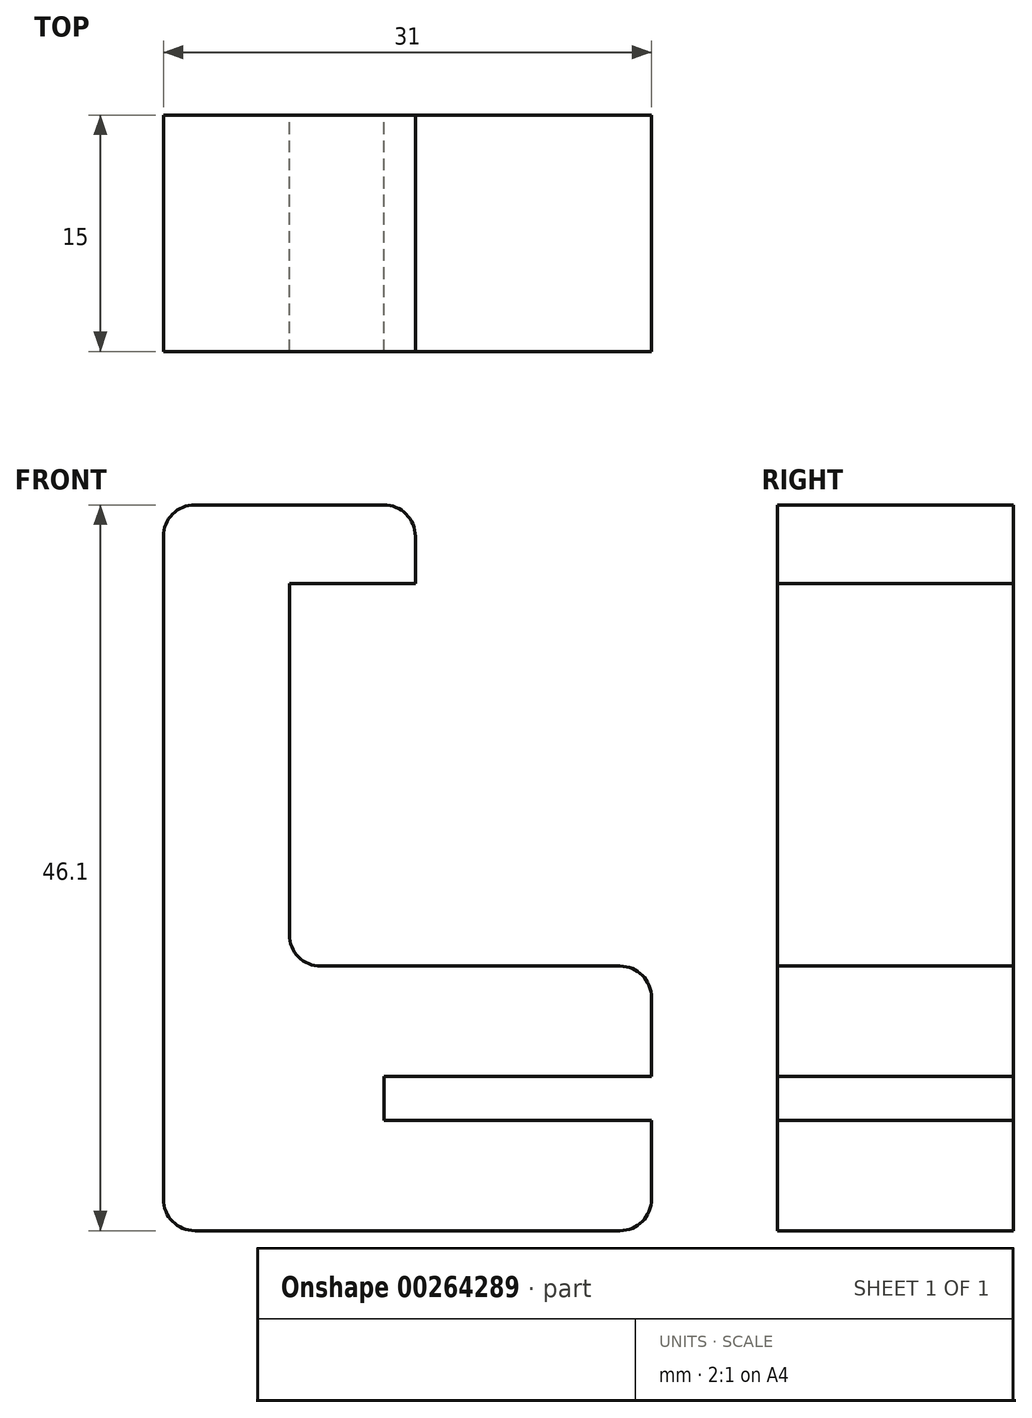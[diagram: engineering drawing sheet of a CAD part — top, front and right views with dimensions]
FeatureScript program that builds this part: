
annotation { "Feature Type Name" : "Feature", "Feature Type Description" : "" }
export const myFeature = defineFeature(function(context is Context, id is Id, definition is map)
    precondition{}
    {
        {
            var Q0;
            Q0=qCreatedBy(makeId("Front.planeOp"),FACE);
            var sketch = newSketch(context, id + "F0", { "sketchPlane" : qUnion([Q0])});
            skLineSegment(sketch, "E0", {"start": v(0, 0) * mm, "end": v(21, 0) * mm});
            skLineSegment(sketch, "E1", {"start": v(23, 2) * mm, "end": v(23, 7) * mm});
            skLineSegment(sketch, "E2", {"start": v(23, 7) * mm, "end": v(6, 7) * mm});
            skLineSegment(sketch, "E3", {"start": v(6, 7) * mm, "end": v(6, 9.8) * mm});
            skLineSegment(sketch, "E4", {"start": v(6, 9.8) * mm, "end": v(23, 9.8) * mm});
            skLineSegment(sketch, "E5", {"start": v(23, 9.8) * mm, "end": v(23, 14.8) * mm});
            skLineSegment(sketch, "E6", {"start": v(21, 16.8) * mm, "end": v(2, 16.8) * mm});
            skLineSegment(sketch, "E7", {"start": v(0, 18.8) * mm, "end": v(0, 29.8) * mm});
            skLineSegment(sketch, "E8", {"start": v(0, 36.8) * mm, "end": v(0, 41.1) * mm});
            skLineSegment(sketch, "E9", {"start": v(0, 41.1) * mm, "end": v(8, 41.1) * mm});
            skLineSegment(sketch, "E10", {"start": v(8, 41.1) * mm, "end": v(8, 44.1) * mm});
            skLineSegment(sketch, "E11", {"start": v(6, 46.1) * mm, "end": v(0, 46.1) * mm});
            skLineSegment(sketch, "E12", {"start": v(0, 46.1) * mm, "end": v(-6, 46.1) * mm});
            skLineSegment(sketch, "E13", {"start": v(-8, 44.1) * mm, "end": v(-8, 2) * mm});
            skLineSegment(sketch, "E14", {"start": v(-6, 0) * mm, "end": v(0, 0) * mm});
            skPoint(sketch, "E15.visualSharp", {"position": v(8, 46.1) * mm});
            skArc(sketch, "E15.filletArc", {"start": v(8, 44.1) * mm, "mid": v(7.41, 45.51) * mm, "end": v(6, 46.1) * mm});
            skPoint(sketch, "E16.visualSharp", {"position": v(-8, 46.1) * mm});
            skArc(sketch, "E16.filletArc", {"start": v(-6, 46.1) * mm, "mid": v(-7.41, 45.51) * mm, "end": v(-8, 44.1) * mm});
            skPoint(sketch, "E17.visualSharp", {"position": v(23, 16.8) * mm});
            skArc(sketch, "E17.filletArc", {"start": v(23, 14.8) * mm, "mid": v(22.41, 16.21) * mm, "end": v(21, 16.8) * mm});
            skPoint(sketch, "E18.visualSharp", {"position": v(23, 0) * mm});
            skArc(sketch, "E18.filletArc", {"start": v(21, 0) * mm, "mid": v(22.41, 0.59) * mm, "end": v(23, 2) * mm});
            skPoint(sketch, "E19.visualSharp", {"position": v(-8, 0) * mm});
            skArc(sketch, "E19.filletArc", {"start": v(-8, 2) * mm, "mid": v(-7.41, 0.59) * mm, "end": v(-6, 0) * mm});
            skPoint(sketch, "E20.visualSharp", {"position": v(0, 31.8) * mm});
            skPoint(sketch, "E21.visualSharp", {"position": v(0, 16.8) * mm});
            skArc(sketch, "E21.filletArc", {"start": v(0, 18.8) * mm, "mid": v(0.59, 17.39) * mm, "end": v(2, 16.8) * mm});
            skLineSegment(sketch, "E22", {"start": v(0, 36.8) * mm, "end": v(0, 29.8) * mm});
            skSolve(sketch);
        }
        {
            var Q0;
            Q0 = qSketchRegion(id + "F0", true);
            extrude(context, id + "F1", {"entities" : qUnion([Q0]), "depth" : 15 * mm});
        }
    });
